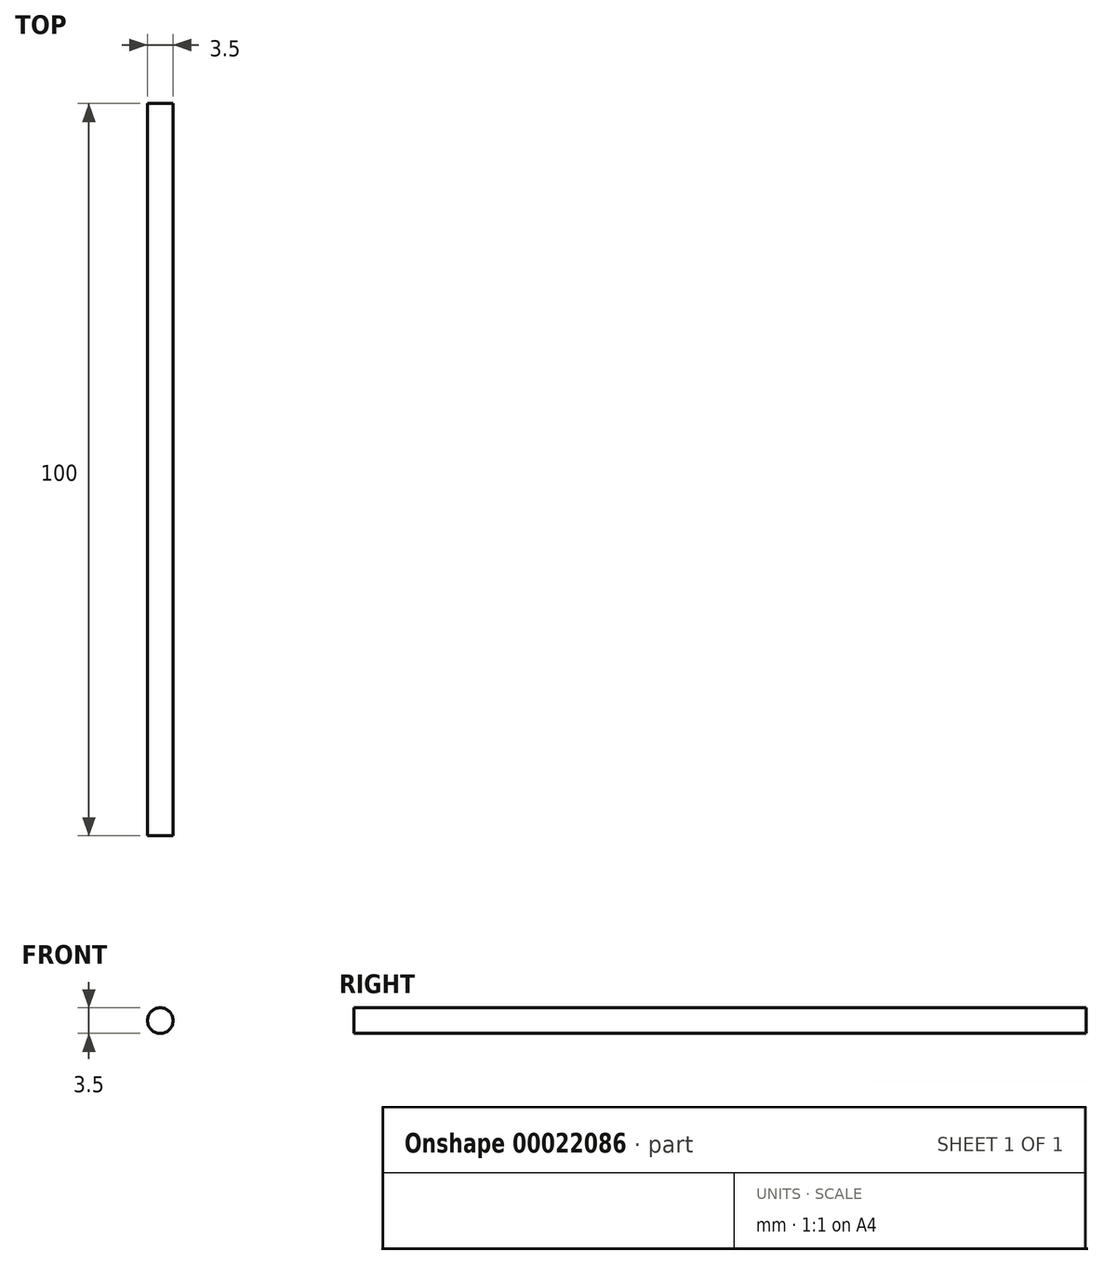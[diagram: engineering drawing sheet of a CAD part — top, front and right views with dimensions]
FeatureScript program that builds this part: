
annotation { "Feature Type Name" : "Feature", "Feature Type Description" : "" }
export const myFeature = defineFeature(function(context is Context, id is Id, definition is map)
    precondition{}
    {
        {
            var Q0;
            Q0=qCreatedBy(makeId("Front.planeOp"),FACE);
            var sketch = newSketch(context, id + "F0", { "sketchPlane" : qUnion([Q0])});
            skCircle(sketch, "E0", {"center": v(0, 0) * mm, "radius": 1.75 * mm});
            skSolve(sketch);
        }
        {
            var Q0;
            Q0=makeQuery(id+"F0.imprint","IMPRINT",FACE,{"disambiguationData":[TD([[makeQuery(id+"F0.imprint","IMPRINT",EDGE,{"derivedFrom":sQuery(id+"F0.wireOp",EDGE,"E0")}),1.0]])]});
            extrude(context, id + "F1", {"entities" : qUnion([Q0]), "depth" : 100 * mm});
        }
    });
